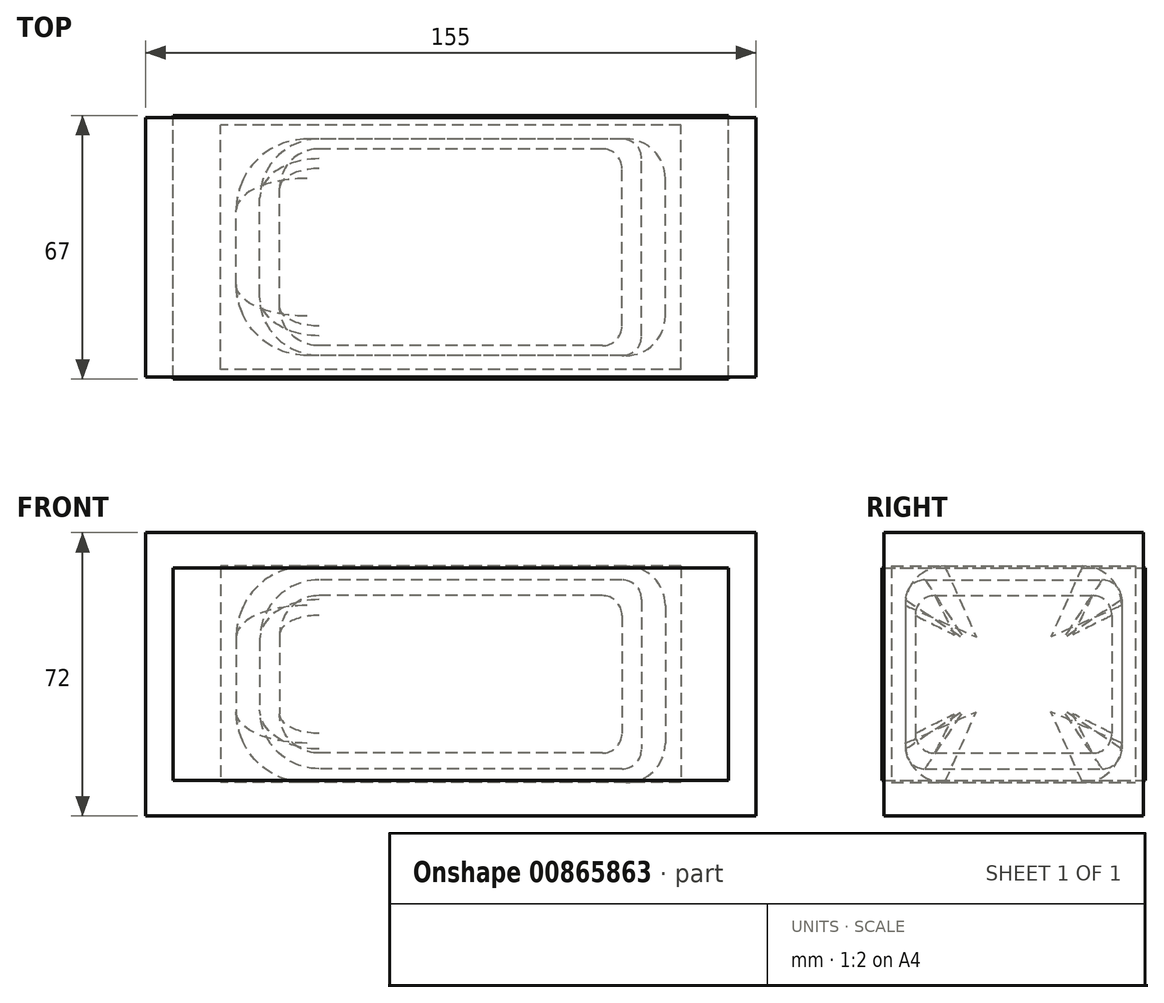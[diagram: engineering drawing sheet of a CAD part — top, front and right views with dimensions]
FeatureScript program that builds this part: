
annotation { "Feature Type Name" : "Feature", "Feature Type Description" : "" }
export const myFeature = defineFeature(function(context is Context, id is Id, definition is map)
    precondition{}
    {
        {
            var Q0;
            Q0=qCreatedBy(makeId("Front.planeOp"),FACE);
            var sketch = newSketch(context, id + "F0", { "sketchPlane" : qUnion([Q0])});
            skLineSegment(sketch, "E0.bottom", {"start": v(48.5, 24) * mm, "end": v(-48.5, 24) * mm});
            skLineSegment(sketch, "E0.top", {"start": v(48.5, -24) * mm, "end": v(-48.5, -24) * mm});
            skLineSegment(sketch, "E0.left", {"start": v(48.5, 24) * mm, "end": v(48.5, -24) * mm});
            skLineSegment(sketch, "E0.right", {"start": v(-48.5, 24) * mm, "end": v(-48.5, -24) * mm});
            skPoint(sketch, "E0.middle", {"position": v(0, 0) * mm});
            skSolve(sketch);
        }
        {
            var Q0;
            Q0=makeQuery(id+"F0.imprint","IMPRINT",FACE,{"disambiguationData":[TD([[makeQuery(id+"F0.imprint","IMPRINT",EDGE,{"derivedFrom":sQuery(id+"F0.wireOp",EDGE,"E0.bottom")}),1.0]])]});
            extrude(context, id + "F1", {"entities" : qUnion([Q0]), "endBound" : BoundingType.SYMMETRIC, "depth" : 55 * mm, "offsetDistance" : 25 * mm});
        }
        {
            var Q0;
            Q0=qCreatedBy(makeId("Front.planeOp"),FACE);
            var sketch = newSketch(context, id + "F2", { "sketchPlane" : qUnion([Q0])});
            skLineSegment(sketch, "E1.bottom", {"start": v(54.5, 27.5) * mm, "end": v(-54.5, 27.5) * mm});
            skLineSegment(sketch, "E1.top", {"start": v(54.5, -27.5) * mm, "end": v(-54.5, -27.5) * mm});
            skLineSegment(sketch, "E1.left", {"start": v(54.5, 27.5) * mm, "end": v(54.5, -27.5) * mm});
            skLineSegment(sketch, "E1.right", {"start": v(-54.5, 27.5) * mm, "end": v(-54.5, -27.5) * mm});
            skPoint(sketch, "E1.middle", {"position": v(0, 0) * mm});
            skSolve(sketch);
        }
        {
            var Q0;
            Q0=qCreatedBy(makeId("Front.planeOp"),FACE);
            var sketch = newSketch(context, id + "F3", { "sketchPlane" : qUnion([Q0])});
            skLineSegment(sketch, "E2.bottom", {"start": v(58.5, 27.5) * mm, "end": v(-58.5, 27.5) * mm});
            skLineSegment(sketch, "E2.top", {"start": v(58.5, -27.5) * mm, "end": v(-58.5, -27.5) * mm});
            skLineSegment(sketch, "E2.left", {"start": v(58.5, 27.5) * mm, "end": v(58.5, -27.5) * mm});
            skLineSegment(sketch, "E2.right", {"start": v(-58.5, 27.5) * mm, "end": v(-58.5, -27.5) * mm});
            skPoint(sketch, "E2.middle", {"position": v(0, 0) * mm});
            skSolve(sketch);
        }
        {
            var Q0;
            Q0=qCreatedBy(makeId("Front.planeOp"),FACE);
            var sketch = newSketch(context, id + "F4", { "sketchPlane" : qUnion([Q0])});
            skLineSegment(sketch, "E3.bottom", {"start": v(70.5, 27) * mm, "end": v(-70.5, 27) * mm});
            skLineSegment(sketch, "E3.top", {"start": v(70.5, -27) * mm, "end": v(-70.5, -27) * mm});
            skLineSegment(sketch, "E3.left", {"start": v(70.5, 27) * mm, "end": v(70.5, -27) * mm});
            skLineSegment(sketch, "E3.right", {"start": v(-70.5, 27) * mm, "end": v(-70.5, -27) * mm});
            skPoint(sketch, "E3.middle", {"position": v(0, 0) * mm});
            skSolve(sketch);
        }
        {
            var Q0;
            Q0 = qSketchRegion(id + "F2", true);
            extrude(context, id + "F5", {"entities" : qUnion([Q0]), "endBound" : BoundingType.SYMMETRIC, "depth" : 55 * mm, "offsetDistance" : 25 * mm});
        }
        {
            var Q0;
            Q0 = qSketchRegion(id + "F3", true);
            extrude(context, id + "F6", {"entities" : qUnion([Q0]), "endBound" : BoundingType.SYMMETRIC, "depth" : 62 * mm, "offsetDistance" : 25 * mm});
        }
        {
            var Q0;
            Q0 = qSketchRegion(id + "F4", true);
            extrude(context, id + "F7", {"entities" : qUnion([Q0]), "endBound" : BoundingType.SYMMETRIC, "depth" : 67 * mm, "offsetDistance" : 25 * mm});
        }
        {
            var Q0;
            Q0=qCreatedBy(makeId("Front.planeOp"),FACE);
            var sketch = newSketch(context, id + "F8", { "sketchPlane" : qUnion([Q0])});
            skLineSegment(sketch, "E4.bottom", {"start": v(77.5, 36) * mm, "end": v(-77.5, 36) * mm});
            skLineSegment(sketch, "E4.top", {"start": v(77.5, -36) * mm, "end": v(-77.5, -36) * mm});
            skLineSegment(sketch, "E4.left", {"start": v(77.5, 36) * mm, "end": v(77.5, -36) * mm});
            skLineSegment(sketch, "E4.right", {"start": v(-77.5, 36) * mm, "end": v(-77.5, -36) * mm});
            skPoint(sketch, "E4.middle", {"position": v(0, 0) * mm});
            skSolve(sketch);
        }
        {
            var Q0;
            Q0 = qSketchRegion(id + "F8", true);
            extrude(context, id + "F9", {"entities" : qUnion([Q0]), "endBound" : BoundingType.SYMMETRIC, "depth" : 66 * mm, "offsetDistance" : 25 * mm});
        }
        {
            var Q0;
            Q0=qCreatedBy(makeId("Front.planeOp"),FACE);
            var sketch = newSketch(context, id + "F10", { "sketchPlane" : qUnion([Q0])});
            skLineSegment(sketch, "E5.bottom", {"start": v(43.5, 20) * mm, "end": v(-43.5, 20) * mm});
            skLineSegment(sketch, "E5.top", {"start": v(43.5, -20) * mm, "end": v(-43.5, -20) * mm});
            skLineSegment(sketch, "E5.left", {"start": v(43.5, 20) * mm, "end": v(43.5, -20) * mm});
            skLineSegment(sketch, "E5.right", {"start": v(-43.5, 20) * mm, "end": v(-43.5, -20) * mm});
            skPoint(sketch, "E5.middle", {"position": v(0, 0) * mm});
            skSolve(sketch);
        }
        {
            var Q0;
            Q0 = qSketchRegion(id + "F10", true);
            extrude(context, id + "F11", {"entities" : qUnion([Q0]), "endBound" : BoundingType.SYMMETRIC, "depth" : 50 * mm, "offsetDistance" : 25 * mm});
        }
        {
            var Q0;
            Q0=makeQuery(id+"F1.opExtrude","CAP_EDGE",EDGE,{"disambiguationData":[OSD([sQuery(id+"F0.wireOp",EDGE,"E0.right")])],"isStart":false});
            var Q1;
            Q1=makeQuery(id+"F1.opExtrude","CAP_EDGE",EDGE,{"disambiguationData":[OSD([sQuery(id+"F0.wireOp",EDGE,"E0.right")])],"isStart":true});
            var Q2;
            Q2=makeQuery(id+"F1.opExtrude","SWEPT_EDGE",EDGE,{"disambiguationData":[OSD([sQuery(id+"F0.wireOp",EDGE,"E0.bottom"),sQuery(id+"F0.wireOp",EDGE,"E0.right")])]});
            var Q3;
            Q3=makeQuery(id+"F1.opExtrude","SWEPT_EDGE",EDGE,{"disambiguationData":[OSD([sQuery(id+"F0.wireOp",EDGE,"E0.top"),sQuery(id+"F0.wireOp",EDGE,"E0.right")])]});
            fillet(context, id + "F12", {"entities" : qUnion([Q0, Q1, Q2, Q3]), "radius" : 15 * mm, "tangentPropagation" : true, "allowEdgeOverflow" : false});
        }
        {
            var Q0;
            Q0=makeQuery(id+"F1.opExtrude","SWEPT_FACE",FACE,{"disambiguationData":[OSD([sQuery(id+"F0.wireOp",EDGE,"E0.left")])]});
            var Q1;
            Q1=makeQuery(id+"F1.opExtrude","CAP_EDGE",EDGE,{"disambiguationData":[OSD([sQuery(id+"F0.wireOp",EDGE,"E0.bottom")])],"isStart":false});
            var Q2;
            Q2=makeQuery(id+"F1.opExtrude","CAP_EDGE",EDGE,{"disambiguationData":[OSD([sQuery(id+"F0.wireOp",EDGE,"E0.top")])],"isStart":false});
            var Q3;
            Q3=makeQuery(id+"F1.opExtrude","CAP_EDGE",EDGE,{"disambiguationData":[OSD([sQuery(id+"F0.wireOp",EDGE,"E0.bottom")])],"isStart":true});
            var Q4;
            Q4=makeQuery(id+"F1.opExtrude","CAP_EDGE",EDGE,{"disambiguationData":[OSD([sQuery(id+"F0.wireOp",EDGE,"E0.top")])],"isStart":true});
            fillet(context, id + "F13", {"entities" : qUnion([Q0, Q1, Q2, Q3, Q4]), "radius" : 5 * mm, "tangentPropagation" : true, "allowEdgeOverflow" : false});
        }
        {
            var Q0;
            Q0=makeQuery(id+"F5.opExtrude","CAP_EDGE",EDGE,{"disambiguationData":[OSD([sQuery(id+"F2.wireOp",EDGE,"E1.bottom")])],"isStart":false});
            var Q1;
            Q1=makeQuery(id+"F5.opExtrude","CAP_EDGE",EDGE,{"disambiguationData":[OSD([sQuery(id+"F2.wireOp",EDGE,"E1.top")])],"isStart":false});
            var Q2;
            Q2=makeQuery(id+"F5.opExtrude","SWEPT_FACE",FACE,{"disambiguationData":[OSD([sQuery(id+"F2.wireOp",EDGE,"E1.left")])]});
            var Q3;
            Q3=makeQuery(id+"F5.opExtrude","CAP_EDGE",EDGE,{"disambiguationData":[OSD([sQuery(id+"F2.wireOp",EDGE,"E1.bottom")])],"isStart":true});
            var Q4;
            Q4=makeQuery(id+"F5.opExtrude","CAP_EDGE",EDGE,{"disambiguationData":[OSD([sQuery(id+"F2.wireOp",EDGE,"E1.top")])],"isStart":true});
            fillet(context, id + "F14", {"entities" : qUnion([Q0, Q1, Q2, Q3, Q4]), "radius" : 10 * mm, "tangentPropagation" : true, "allowEdgeOverflow" : false});
        }
        {
            var Q0;
            Q0=makeQuery(id+"F5.opExtrude","SWEPT_EDGE",EDGE,{"disambiguationData":[OSD([sQuery(id+"F2.wireOp",EDGE,"E1.bottom"),sQuery(id+"F2.wireOp",EDGE,"E1.right")])]});
            fillet(context, id + "F15", {"entities" : qUnion([Q0]), "radius" : 18 * mm, "tangentPropagation" : true, "allowEdgeOverflow" : false});
        }
        {
            var Q0;
            Q0=makeQuery(id+"F11.opExtrude","SWEPT_FACE",FACE,{"disambiguationData":[OSD([sQuery(id+"F10.wireOp",EDGE,"E5.right")])]});
            fillet(context, id + "F16", {"entities" : qUnion([Q0]), "radius" : 10 * mm, "tangentPropagation" : true, "allowEdgeOverflow" : false});
        }
        {
            var Q0;
            Q0=makeQuery(id+"F11.opExtrude","SWEPT_FACE",FACE,{"disambiguationData":[OSD([sQuery(id+"F10.wireOp",EDGE,"E5.left")])]});
            var Q1;
            Q1=makeQuery(id+"F11.opExtrude","CAP_EDGE",EDGE,{"disambiguationData":[OSD([sQuery(id+"F10.wireOp",EDGE,"E5.bottom")])],"isStart":false});
            var Q2;
            Q2=makeQuery(id+"F11.opExtrude","CAP_EDGE",EDGE,{"disambiguationData":[OSD([sQuery(id+"F10.wireOp",EDGE,"E5.top")])],"isStart":false});
            var Q3;
            Q3=makeQuery(id+"F11.opExtrude","CAP_EDGE",EDGE,{"disambiguationData":[OSD([sQuery(id+"F10.wireOp",EDGE,"E5.bottom")])],"isStart":true});
            var Q4;
            Q4=makeQuery(id+"F11.opExtrude","CAP_EDGE",EDGE,{"disambiguationData":[OSD([sQuery(id+"F10.wireOp",EDGE,"E5.top")])],"isStart":true});
            fillet(context, id + "F17", {"entities" : qUnion([Q0, Q1, Q2, Q3, Q4]), "radius" : 5 * mm, "tangentPropagation" : true, "allowEdgeOverflow" : false});
        }
    });
